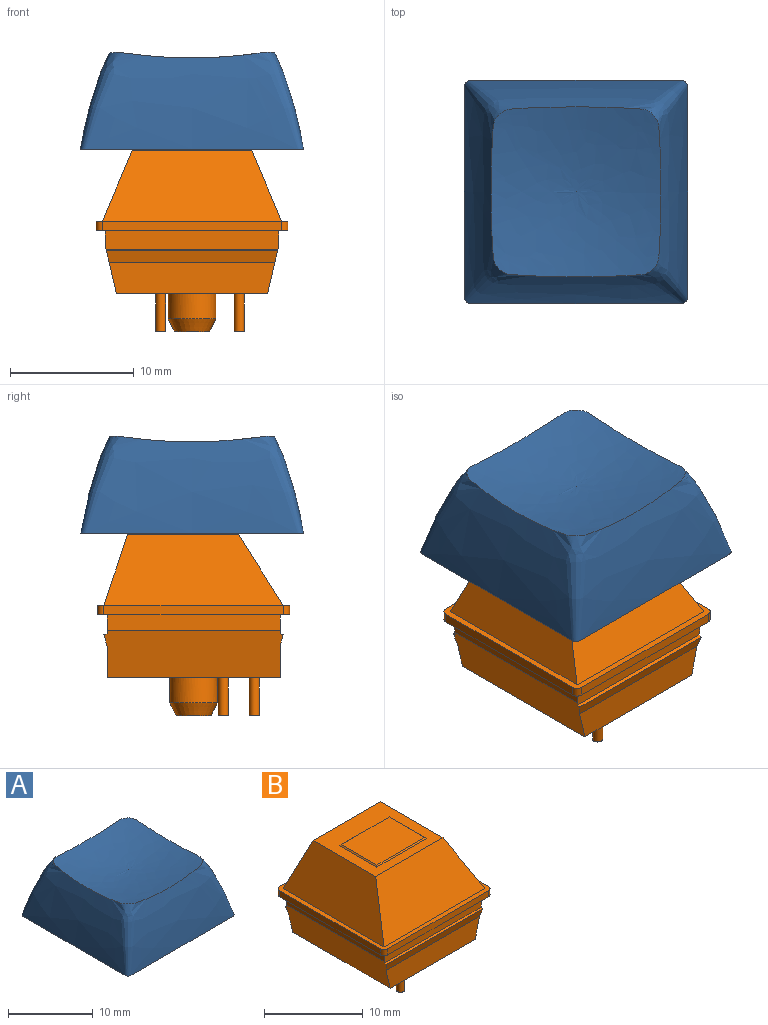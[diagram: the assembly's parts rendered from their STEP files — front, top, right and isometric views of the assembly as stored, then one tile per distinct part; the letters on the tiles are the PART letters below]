
ASSEMBLY  parts=2 mates=1
PART A: 29 faces, bbox 20x20x10 mm
  f0: revolved ~17.19x17.19mm, area 272mm2, adj f4,f5,f6,f7,f8,f24
  f1: plane 18.82x18.82mm, normal (0,0,-1), area 68.7mm2, adj f3,f4,f5,f6,f7,f8
  f2: revolved ~13.7x13.68mm, area 149.4mm2, adj f3
  f3: bspline ~18x18mm, area 498mm2, adj f1,f2
  f4: offset ~10.76x10mm, area 48.2mm2, adj f0,f1,f5,f8
  f5: offset ~10.76x10mm, area 48.2mm2, adj f0,f1,f4,f6
  f6: offset ~19.58x10mm, area 99.3mm2, adj f0,f1,f5,f7
  f7: offset ~19.58x10mm, area 99.3mm2, adj f0,f1,f6,f8
  f8: offset ~19.58x10mm, area 99.3mm2, adj f0,f1,f4,f7
  f9: plane 5.83x1.91mm, normal (0,1,0), area 6.7mm2, adj f10,f18,f20,f23,f28
  f10: plane 5.83x1.91mm, normal (1,0,0), area 6.7mm2, adj f9,f11,f18,f23,f27
  f11: plane 5.42x1.91mm, normal (0,1,0), area 8.2mm2, adj f10,f12,f23,f27
  f12: plane 5.83x1.91mm, normal (-1,0,0), area 6.7mm2, adj f11,f13,f18,f23,f27
  f13: plane 5.83x1.91mm, normal (0,1,0), area 6.7mm2, adj f12,f14,f18,f23,f26
  f14: plane 5.42x1.91mm, normal (-1,0,0), area 8.2mm2, adj f13,f15,f23,f26
  f15: plane 5.83x1.91mm, normal (0,-1,0), area 6.7mm2, adj f14,f16,f18,f23,f26
  f16: plane 5.83x1.91mm, normal (-1,0,0), area 6.7mm2, adj f15,f17,f18,f23,f25
  f17: plane 5.42x1.91mm, normal (0,-1,0), area 8.2mm2, adj f16,f21,f23,f25
  f18: plane 5.5x5.5mm, normal (0,0,-1), area 10.3mm2, adj f9,f10,f12,f13,f15,f16,f19,f21
  f19: cylinder r=2.75mm len=5.5mm, axis (0,0,-1), area 67.8mm2, adj f18,f24
  f20: plane 5.19x1.68mm, normal (1,0,0), area 8.2mm2, adj f9,f22,f23,f28
  f21: plane 5.83x1.91mm, normal (1,0,0), area 6.7mm2, adj f17,f18,f22,f23,f25
  f22: plane 5.83x1.91mm, normal (0,-1,0), area 6.7mm2, adj f18,f20,f21,f23,f28
  f23: revolved ~4.3x4.3mm, area 11.4mm2, adj f9,f10,f11,f12,f13,f14,f15,f16
  f24: torus R=4.75mm, axis (0,0,-1), area 59.8mm2, adj f0,f19
  f25: cylinder r=0.5mm len=1.6mm, axis (-1,0,0), area 1.3mm2, adj f16,f17,f18,f21
  f26: cylinder r=0.5mm len=1.6mm, axis (0,1,0), area 1.3mm2, adj f13,f14,f15,f18
  f27: cylinder r=0.5mm len=1.6mm, axis (1,0,0), area 1.3mm2, adj f10,f11,f12,f18
  f28: cylinder r=0.5mm len=1.6mm, axis (0,-1,0), area 1.3mm2, adj f9,f18,f20,f22
PART B: 40 faces, bbox 15.5x15.5x14.7 mm
  f0: plane 6.86x5.08mm, normal (0,0,1), area 34.8mm2, adj f5,f10,f21,f23
  f1: plane 13.97x12.19mm, normal (0,0,-1), area 157.7mm2, adj f6,f9,f28,f30,f33,f35,f37
  f2: plane 14.48x0.76mm, normal (0,-1,0), area 11mm2, adj f15,f17,f19,f20
  f3: plane 14.48x0.76mm, normal (0,1,0), area 11mm2, adj f16,f18,f19,f20
  f4: plane 14.48x5.72mm, normal (-0.92,0,0.39), area 72.7mm2, adj f11,f20,f22,f24
  f5: plane 5.33x0.13mm, normal (-0.71,0,0.71), area 0.9mm2, adj f0,f11,f21,f23
  f6: plane 14.48x3.81mm, normal (-0.97,0,-0.23), area 54.9mm2, adj f1,f7,f25,f26,f27,f28,f29,f30
  f7: plane 13.97x1.27mm, normal (-1,0,0), area 17.7mm2, adj f6,f19,f25,f29
  f8: plane 13.97x1.27mm, normal (1,0,0), area 17.7mm2, adj f9,f19,f25,f29
  f9: plane 14.48x3.81mm, normal (0.97,0,-0.23), area 54.9mm2, adj f1,f8,f25,f26,f27,f28,f29,f30
  f10: plane 5.33x0.13mm, normal (0.71,0,0.71), area 0.9mm2, adj f0,f11,f21,f23
  f11: plane 9.65x8.97mm, normal (0,0,1), area 48.6mm2, adj f4,f5,f10,f12,f21,f22,f23,f24
  f12: plane 14.48x5.72mm, normal (0.92,0,0.39), area 72.7mm2, adj f11,f20,f22,f24
  f13: plane 14.48x0.76mm, normal (1,0,0), area 11mm2, adj f17,f18,f19,f20
  f14: plane 14.48x0.76mm, normal (-1,0,0), area 11mm2, adj f15,f16,f19,f20
  f15: cylinder r=0.51mm len=0.76mm, axis (0,0,-1), area 0.6mm2, adj f2,f14,f19,f20
  f16: cylinder r=0.51mm len=0.76mm, axis (0,0,-1), area 0.6mm2, adj f3,f14,f19,f20
  f17: cylinder r=0.51mm len=0.76mm, axis (0,0,-1), area 0.6mm2, adj f2,f13,f19,f20
  f18: cylinder r=0.51mm len=0.76mm, axis (0,0,-1), area 0.6mm2, adj f3,f13,f19,f20
  f19: plane 15.49x15.49mm, normal (0,0,-1), area 44.7mm2, adj f2,f3,f7,f8,f13,f14,f15,f16
  f20: plane 15.49x15.49mm, normal (0,0,1), area 30.2mm2, adj f2,f3,f4,f12,f13,f14,f15,f16
  f21: plane 7.11x0.13mm, normal (0,0.71,0.71), area 1.3mm2, adj f0,f5,f10,f11
  f22: plane 14.48x5.72mm, normal (0,0.95,0.32), area 72.7mm2, adj f4,f11,f12,f20
  f23: plane 7.11x0.13mm, normal (0,-0.71,0.71), area 1.3mm2, adj f0,f5,f10,f11
  f24: plane 14.48x5.72mm, normal (0,-0.85,0.53), area 81.5mm2, adj f4,f11,f12,f20
  f25: plane 13.97x1.52mm, normal (0,-1,0), area 21.3mm2, adj f6,f7,f8,f9,f19,f26
  f26: plane 13.85x0.25mm, normal (0,-0.26,0.97), area 3.6mm2, adj f6,f9,f25,f27
  f27: plane 13.82x0.95mm, normal (0,-0.97,-0.26), area 13.3mm2, adj f6,f9,f26,f28
  f28: plane 13.38x2.54mm, normal (0,-1,0), area 32.5mm2, adj f1,f6,f9,f27
  f29: plane 13.97x1.52mm, normal (0,1,0), area 21.3mm2, adj f6,f7,f8,f9,f19,f32
  f30: plane 13.38x2.54mm, normal (0,1,0), area 32.5mm2, adj f1,f6,f9,f31
  f31: plane 13.82x0.95mm, normal (0,0.97,-0.26), area 13.3mm2, adj f6,f9,f30,f32
  f32: plane 13.85x0.25mm, normal (0,0.26,0.97), area 3.6mm2, adj f6,f9,f29,f31
  f33: cylinder r=1.92mm len=3.84mm, axis (0,0,1), area 24.5mm2, adj f1,f39
  f34: plane 2.82x2.82mm, normal (0,0,-1), area 6.2mm2, adj f39
  f35: cylinder r=0.41mm len=3.05mm, axis (0,0,1), area 7.8mm2, adj f1,f36
  f36: plane 0.81x0.81mm, normal (0,0,-1), area 0.5mm2, adj f35
  f37: cylinder r=0.41mm len=3.05mm, axis (0,0,1), area 7.8mm2, adj f1,f38
  f38: plane 0.81x0.81mm, normal (0,0,-1), area 0.5mm2, adj f37
  f39: cone r=1.41mm half-angle=26.6deg, axis (0,0,1), area 11.9mm2, adj f33,f34
PLACE A t=(-9,0.13,11.68)mm
PLACE B at identity
MATE fastened A.f19 <-> B.f0  axis (0,0,-1) through (0,0.13,11.68)mm
